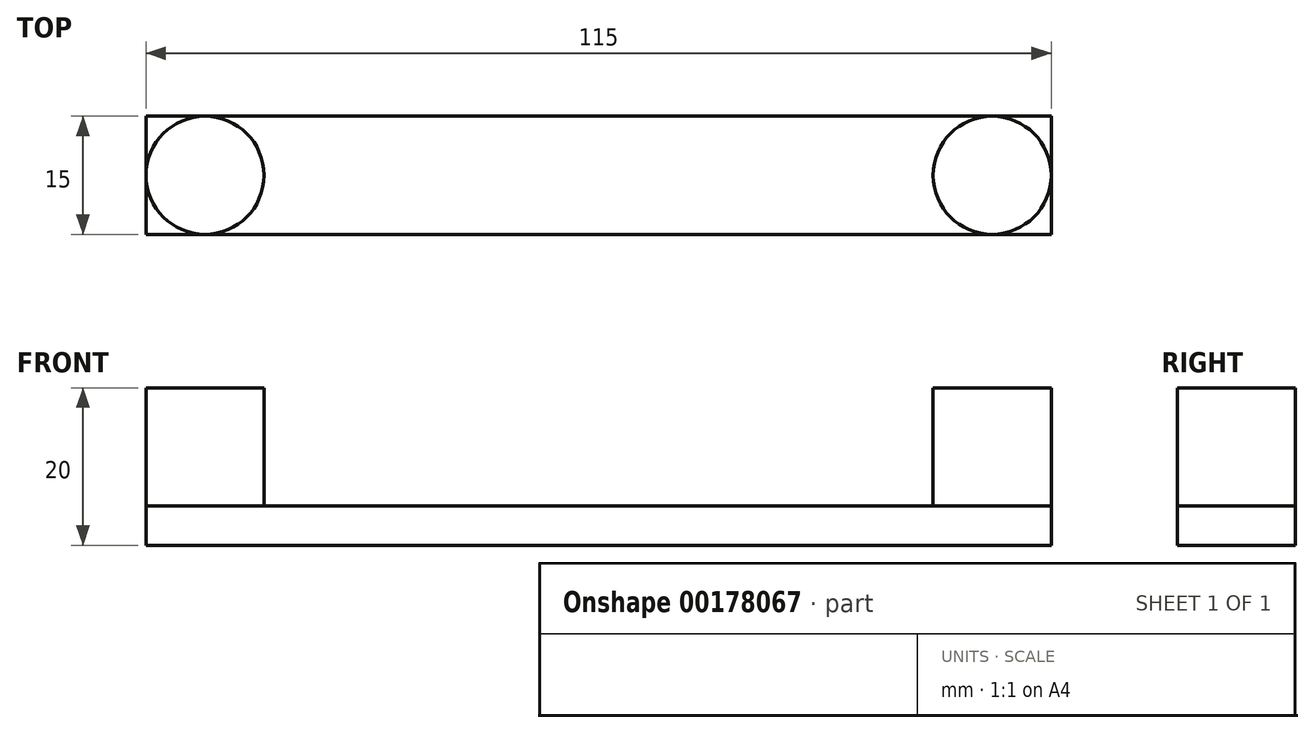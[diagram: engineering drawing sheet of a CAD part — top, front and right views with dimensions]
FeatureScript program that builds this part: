
annotation { "Feature Type Name" : "Feature", "Feature Type Description" : "" }
export const myFeature = defineFeature(function(context is Context, id is Id, definition is map)
    precondition{}
    {
        {
            var Q0;
            Q0=qCreatedBy(makeId("Top.planeOp"),FACE);
            var sketch = newSketch(context, id + "F0", { "sketchPlane" : qUnion([Q0])});
            skLineSegment(sketch, "E0.bottom", {"start": v(57.5, 7.5) * mm, "end": v(-57.5, 7.5) * mm});
            skLineSegment(sketch, "E0.top", {"start": v(57.5, -7.5) * mm, "end": v(-57.5, -7.5) * mm});
            skLineSegment(sketch, "E0.left", {"start": v(57.5, 7.5) * mm, "end": v(57.5, -7.5) * mm});
            skLineSegment(sketch, "E0.right", {"start": v(-57.5, 7.5) * mm, "end": v(-57.5, -7.5) * mm});
            skPoint(sketch, "E0.middle", {"position": v(0, 0) * mm});
            skSolve(sketch);
        }
        {
            var Q0;
            Q0 = qSketchRegion(id + "F0", true);
            extrude(context, id + "F1", {"entities" : qUnion([Q0]), "depth" : 5 * mm});
        }
        {
            var Q0;
            Q0=makeQuery(id+"F1.opExtrude","CAP_FACE",FACE,{"disambiguationData":[OSD([sQuery(id+"F0.wireOp",EDGE,"E0.bottom"),sQuery(id+"F0.wireOp",EDGE,"E0.top"),sQuery(id+"F0.wireOp",EDGE,"E0.left"),sQuery(id+"F0.wireOp",EDGE,"E0.right")])],"isStart":false});
            var sketch = newSketch(context, id + "F2", { "sketchPlane" : qUnion([Q0])});
            skLineSegment(sketch, "E1", {"start": v(-57.5, 0) * mm, "end": v(-50, 0) * mm});
            skCircle(sketch, "E2", {"center": v(-50, 0) * mm, "radius": 7.5 * mm});
            skLineSegment(sketch, "E3", {"start": v(57.5, 0) * mm, "end": v(50, 0) * mm});
            skPoint(sketch, "E3.endSnap0", {"position": v(57.5, 0) * mm});
            skCircle(sketch, "E4", {"center": v(50, 0) * mm, "radius": 7.5 * mm});
            skSolve(sketch);
        }
        {
            var Q0;
            Q0 = qSketchRegion(id + "F2", true);
            extrude(context, id + "F3", {"entities" : qUnion([Q0]), "operationType" : NewBodyOperationType.ADD, "depth" : 15 * mm});
        }
    });
